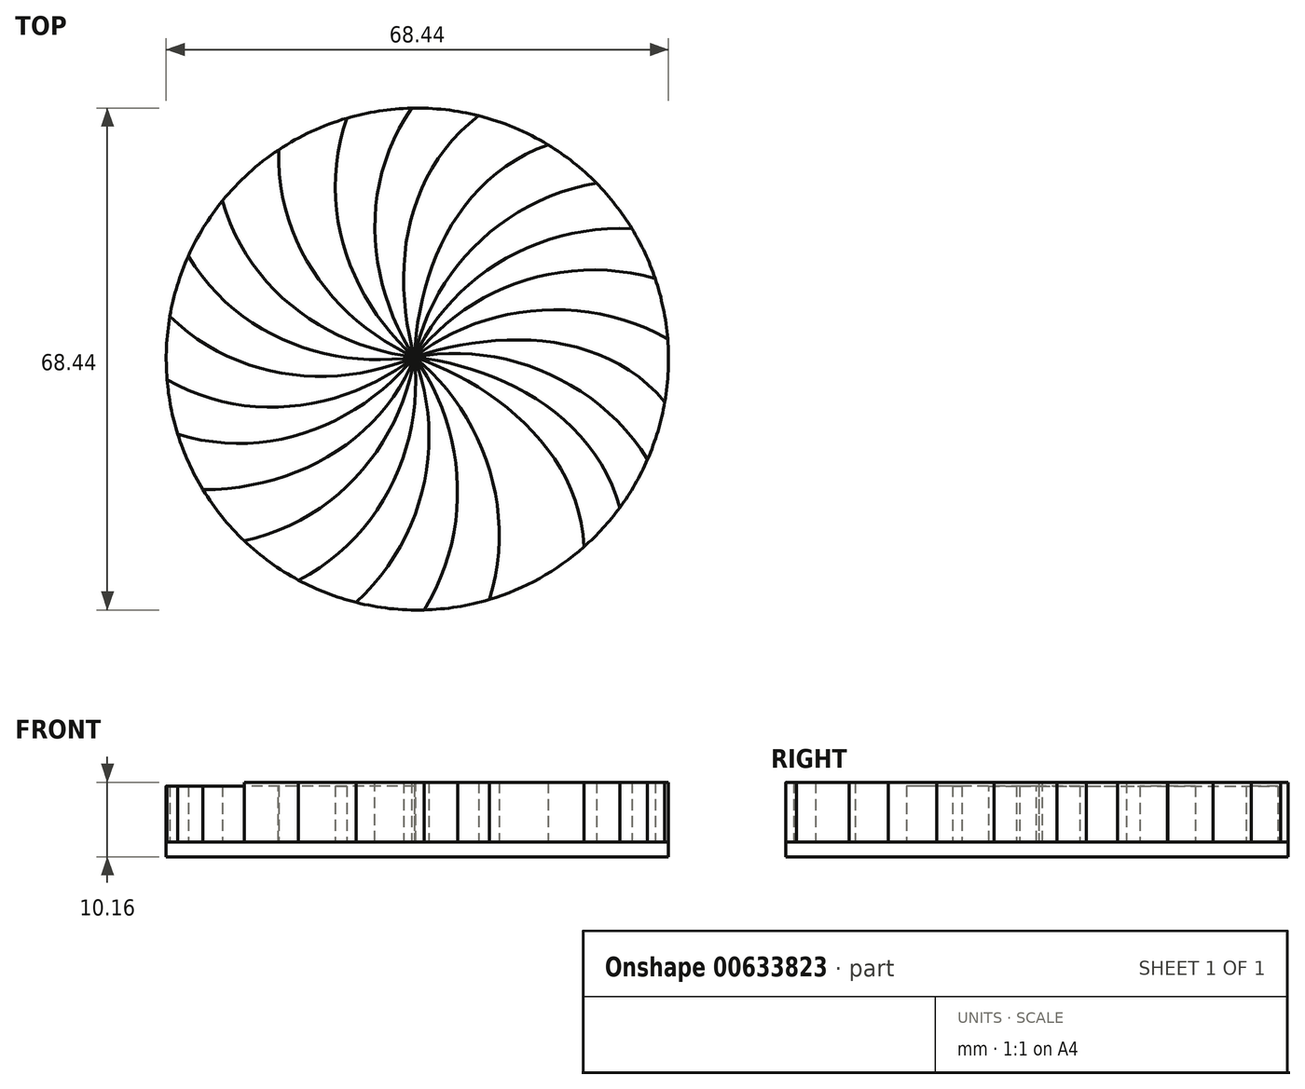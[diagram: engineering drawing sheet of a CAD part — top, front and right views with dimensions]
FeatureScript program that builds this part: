
annotation { "Feature Type Name" : "Feature", "Feature Type Description" : "" }
export const myFeature = defineFeature(function(context is Context, id is Id, definition is map)
    precondition{}
    {
        {
            var Q0;
            Q0=qCreatedBy(makeId("Top.planeOp"),FACE);
            var sketch = newSketch(context, id + "F0", { "sketchPlane" : qUnion([Q0])});
            skCircle(sketch, "E0", {"center": v(0, 0) * mm, "radius": 34.22 * mm});
            skSolve(sketch);
        }
        {
            var Q0;
            Q0=makeQuery(id+"F0.imprint","IMPRINT",FACE,{"disambiguationData":[TD([[makeQuery(id+"F0.imprint","IMPRINT",EDGE,{"derivedFrom":sQuery(id+"F0.wireOp",EDGE,"E0")}),1.0]])]});
            extrude(context, id + "F1", {"entities" : qUnion([Q0]), "depth" : 2.03 * mm, "offsetDistance" : 25.4 * mm});
        }
        {
            var Q0;
            Q0=makeQuery(id+"F1.opExtrude","CAP_FACE",FACE,{"disambiguationData":[OSD([sQuery(id+"F0.wireOp",EDGE,"E0")])],"isStart":false});
            var sketch = newSketch(context, id + "F2", { "sketchPlane" : qUnion([Q0])});
            skFitSpline(sketch, "E1", {"points": [v(-0.38, 0.28) * mm, v(-18.88, 29) * mm], "startDerivative": vector(-32.94, 14.89) * mm, "endDerivative": vector(1.8, 38.8) * mm});
            skFitSpline(sketch, "E2", {"points": [v(-0.38, 0.28) * mm, v(-9.47, 33.21) * mm], "startDerivative": vector(-27, 24.04) * mm, "endDerivative": vector(13.3, 36.5) * mm});
            skFitSpline(sketch, "E3", {"points": [v(-0.38, 0.28) * mm, v(8.37, 33.18) * mm], "startDerivative": vector(-9.77, 34.8) * mm, "endDerivative": vector(30.88, 23.56) * mm});
            skFitSpline(sketch, "E4", {"points": [v(-0.38, 0.28) * mm, v(-26.71, 22.05) * mm], "startDerivative": vector(-35.9, 4.21) * mm, "endDerivative": vector(-10.04, 37.53) * mm});
            skFitSpline(sketch, "E5", {"points": [v(-0.38, 0.28) * mm, v(17.81, 29.22) * mm], "startDerivative": vector(1.4, 36.12) * mm, "endDerivative": vector(36.63, 12.94) * mm});
            skFitSpline(sketch, "E6", {"points": [v(-0.38, 0.28) * mm, v(-31.46, 14.47) * mm], "startDerivative": vector(-35.76, -5.25) * mm, "endDerivative": vector(-19.43, 33.63) * mm});
            skFitSpline(sketch, "E7", {"points": [v(-0.38, 0.28) * mm, v(-34.04, 6.17) * mm], "startDerivative": vector(-33.28, -14.1) * mm, "endDerivative": vector(-27.29, 27.65) * mm});
            skFitSpline(sketch, "E8", {"points": [v(-0.38, 0.28) * mm, v(9.78, -32.94) * mm], "startDerivative": vector(27.96, -22.9) * mm, "endDerivative": vector(-11.79, -37.01) * mm});
            skFitSpline(sketch, "E9", {"points": [v(-0.38, 0.28) * mm, v(0.75, -34.44) * mm], "startDerivative": vector(21.08, -29.36) * mm, "endDerivative": vector(-20.96, -32.7) * mm});
            skFitSpline(sketch, "E10", {"points": [v(-0.38, 0.28) * mm, v(-8.37, -33.18) * mm], "startDerivative": vector(12.76, -33.82) * mm, "endDerivative": vector(-28.71, -26.16) * mm});
            skFitSpline(sketch, "E11", {"points": [v(-0.38, 0.28) * mm, v(-16.18, -30.15) * mm], "startDerivative": vector(3.57, -35.97) * mm, "endDerivative": vector(-34.5, -17.84) * mm});
            skFitSpline(sketch, "E12", {"points": [v(-0.38, 0.28) * mm, v(-23.6, -24.78) * mm], "startDerivative": vector(-5.86, -35.67) * mm, "endDerivative": vector(-37.95, -8.3) * mm});
            skFitSpline(sketch, "E13", {"points": [v(-0.38, 0.28) * mm, v(-29.22, -17.81) * mm], "startDerivative": vector(-13.16, -33.66) * mm, "endDerivative": vector(-38.84, -0.2) * mm});
            skFitSpline(sketch, "E14", {"points": [v(-0.38, 0.28) * mm, v(-34.43, -2.6) * mm], "startDerivative": vector(-28.6, -22.1) * mm, "endDerivative": vector(-33.42, 19.79) * mm});
            skFitSpline(sketch, "E15", {"points": [v(-0.38, 0.28) * mm, v(-32.92, -10.16) * mm], "startDerivative": vector(-22.9, -27.96) * mm, "endDerivative": vector(-37.01, 11.79) * mm});
            skFitSpline(sketch, "E16", {"points": [v(-0.38, 0.28) * mm, v(24.4, 24) * mm], "startDerivative": vector(7.38, 35.38) * mm, "endDerivative": vector(38.27, 6.66) * mm});
            skFitSpline(sketch, "E17", {"points": [v(-0.38, 0.28) * mm, v(29.24, 17.78) * mm], "startDerivative": vector(14.89, 32.94) * mm, "endDerivative": vector(38.8, -1.8) * mm});
            skFitSpline(sketch, "E18", {"points": [v(-0.38, 0.28) * mm, v(32.4, 11) * mm], "startDerivative": vector(21.88, 28.77) * mm, "endDerivative": vector(37.42, -10.44) * mm});
            skFitSpline(sketch, "E19", {"points": [v(-0.38, 0.28) * mm, v(33.72, -5.84) * mm], "startDerivative": vector(34.32, 11.35) * mm, "endDerivative": vector(24.95, -29.77) * mm});
            skFitSpline(sketch, "E20", {"points": [v(-0.38, 0.28) * mm, v(34.44, 2.56) * mm], "startDerivative": vector(28.46, 22.29) * mm, "endDerivative": vector(33.55, -19.58) * mm});
            skFitSpline(sketch, "E21", {"points": [v(-0.38, 0.28) * mm, v(31.38, -13.66) * mm], "startDerivative": vector(35.52, 6.7) * mm, "endDerivative": vector(20.78, -32.82) * mm});
            skFitSpline(sketch, "E22", {"points": [v(-0.38, 0.28) * mm, v(27.57, -20.27) * mm], "startDerivative": vector(35.9, -4.22) * mm, "endDerivative": vector(10.02, -37.53) * mm});
            skFitSpline(sketch, "E23", {"points": [v(-0.38, 0.28) * mm, v(22.7, -25.72) * mm], "startDerivative": vector(34.1, -11.96) * mm, "endDerivative": vector(1.58, -38.81) * mm});
            skFitSpline(sketch, "E24", {"points": [v(-0.38, 0.28) * mm, v(17, -29.33) * mm], "startDerivative": vector(31.51, -17.7) * mm, "endDerivative": vector(-5.18, -38.5) * mm});
            skFitSpline(sketch, "E25", {"points": [v(-0.38, 0.28) * mm, v(-0.63, 34.44) * mm], "startDerivative": vector(-19.85, 30.2) * mm, "endDerivative": vector(22.3, 31.81) * mm});
            skSolve(sketch);
        }
        {
            var Q0;
            {var subQ1=sQuery(id+"F2.wireOp",EDGE,"E7");var subQ3=makeQuery(id+"F1.opExtrude","CAP_EDGE",EDGE,{"disambiguationData":[OSD([sQuery(id+"F0.wireOp",EDGE,"E0")])],"isStart":false});var subQ4=makeQuery(id+"F2.imprint","INTERSECT",VERTEX,{"derivedFrom":[subQ3,subQ1]});Q0=makeQuery(id+"F2.imprint","IMPRINT",FACE,{"disambiguationData":[TD([[makeQuery(id+"F2.imprint","IMPRINT",EDGE,{"disambiguationData":[TD([[subQ4,-1.0]])],"derivedFrom":subQ3}),1.0]])]});}
            var Q1;
            {var subQ1=sQuery(id+"F2.wireOp",EDGE,"E4");var subQ3=makeQuery(id+"F1.opExtrude","CAP_EDGE",EDGE,{"disambiguationData":[OSD([sQuery(id+"F0.wireOp",EDGE,"E0")])],"isStart":false});var subQ4=makeQuery(id+"F2.imprint","INTERSECT",VERTEX,{"derivedFrom":[subQ3,subQ1]});Q1=makeQuery(id+"F2.imprint","IMPRINT",FACE,{"disambiguationData":[TD([[makeQuery(id+"F2.imprint","IMPRINT",EDGE,{"disambiguationData":[TD([[subQ4,-1.0]])],"derivedFrom":subQ3}),1.0]])]});}
            var Q2;
            {var subQ1=sQuery(id+"F2.wireOp",EDGE,"E1");var subQ3=makeQuery(id+"F1.opExtrude","CAP_EDGE",EDGE,{"disambiguationData":[OSD([sQuery(id+"F0.wireOp",EDGE,"E0")])],"isStart":false});var subQ4=makeQuery(id+"F2.imprint","INTERSECT",VERTEX,{"derivedFrom":[subQ3,subQ1]});Q2=makeQuery(id+"F2.imprint","IMPRINT",FACE,{"disambiguationData":[TD([[makeQuery(id+"F2.imprint","IMPRINT",EDGE,{"disambiguationData":[TD([[subQ4,1.0]])],"derivedFrom":subQ3}),1.0]])]});}
            var Q3;
            {var subQ1=sQuery(id+"F2.wireOp",EDGE,"E13");var subQ3=makeQuery(id+"F1.opExtrude","CAP_EDGE",EDGE,{"disambiguationData":[OSD([sQuery(id+"F0.wireOp",EDGE,"E0")])],"isStart":false});var subQ4=makeQuery(id+"F2.imprint","INTERSECT",VERTEX,{"derivedFrom":[subQ3,subQ1]});Q3=makeQuery(id+"F2.imprint","IMPRINT",FACE,{"disambiguationData":[TD([[makeQuery(id+"F2.imprint","IMPRINT",EDGE,{"disambiguationData":[TD([[subQ4,1.0]])],"derivedFrom":subQ3}),1.0]])]});}
            var Q4;
            Q4=sQuery(id+"F2.wireOp",EDGE,"E16");
            var Q5;
            Q5=sQuery(id+"F2.wireOp",EDGE,"E5");
            var Q6;
            Q6=sQuery(id+"F2.wireOp",EDGE,"E3");
            var Q7;
            Q7=sQuery(id+"F2.wireOp",EDGE,"E25");
            var Q8;
            Q8=sQuery(id+"F2.wireOp",EDGE,"E2");
            var Q9;
            Q9=sQuery(id+"F2.wireOp",EDGE,"E1");
            var Q10;
            Q10=sQuery(id+"F2.wireOp",EDGE,"E4");
            var Q11;
            Q11=sQuery(id+"F2.wireOp",EDGE,"E6");
            var Q12;
            Q12=sQuery(id+"F2.wireOp",EDGE,"E7");
            var Q13;
            Q13=sQuery(id+"F2.wireOp",EDGE,"E14");
            var Q14;
            Q14=sQuery(id+"F2.wireOp",EDGE,"E15");
            var Q15;
            Q15=sQuery(id+"F2.wireOp",EDGE,"E13");
            var Q16;
            Q16=sQuery(id+"F2.wireOp",EDGE,"E12");
            var Q17;
            Q17=sQuery(id+"F2.wireOp",EDGE,"E11");
            var Q18;
            Q18=sQuery(id+"F2.wireOp",EDGE,"E10");
            var Q19;
            Q19=sQuery(id+"F2.wireOp",EDGE,"E9");
            var Q20;
            Q20=sQuery(id+"F2.wireOp",EDGE,"E8");
            var Q21;
            Q21=sQuery(id+"F2.wireOp",EDGE,"E24");
            var Q22;
            Q22=sQuery(id+"F2.wireOp",EDGE,"E23");
            var Q23;
            Q23=sQuery(id+"F2.wireOp",EDGE,"E22");
            var Q24;
            Q24=sQuery(id+"F2.wireOp",EDGE,"E21");
            var Q25;
            Q25=sQuery(id+"F2.wireOp",EDGE,"E19");
            var Q26;
            Q26=sQuery(id+"F2.wireOp",EDGE,"E20");
            var Q27;
            Q27=sQuery(id+"F2.wireOp",EDGE,"E18");
            var Q28;
            Q28=sQuery(id+"F2.wireOp",EDGE,"E17");
            extrude(context, id + "F3", {"entities" : qUnion([Q0, Q1, Q2, Q3]), "surfaceEntities" : qUnion([Q4, Q5, Q6, Q7, Q8, Q9, Q10, Q11, Q12, Q13, Q14, Q15, Q16, Q17, Q18, Q19, Q20, Q21, Q22, Q23, Q24, Q25, Q26, Q27, Q28]), "depth" : 7.62 * mm, "offsetDistance" : 25.4 * mm});
        }
        {
            var Q0;
            {var subQ0=sQuery(id+"F2.wireOp",EDGE,"E5");Q0=makeQuery(id+"F2.imprint","IMPRINT",FACE,{"disambiguationData":[TD([[makeQuery(id+"F2.imprint","IMPRINT",EDGE,{"derivedFrom":subQ0}),-1.0]])]});}
            var Q1;
            {var subQ0=sQuery(id+"F2.wireOp",EDGE,"E3");Q1=makeQuery(id+"F2.imprint","IMPRINT",FACE,{"disambiguationData":[TD([[makeQuery(id+"F2.imprint","IMPRINT",EDGE,{"derivedFrom":subQ0}),1.0]])]});}
            var Q2;
            {var subQ0=sQuery(id+"F2.wireOp",EDGE,"E17");Q2=makeQuery(id+"F2.imprint","IMPRINT",FACE,{"disambiguationData":[TD([[makeQuery(id+"F2.imprint","IMPRINT",EDGE,{"derivedFrom":subQ0}),-1.0]])]});}
            var Q3;
            {var subQ0=sQuery(id+"F2.wireOp",EDGE,"E19");Q3=makeQuery(id+"F2.imprint","IMPRINT",FACE,{"disambiguationData":[TD([[makeQuery(id+"F2.imprint","IMPRINT",EDGE,{"derivedFrom":subQ0}),1.0]])]});}
            var Q4;
            {var subQ0=sQuery(id+"F2.wireOp",EDGE,"E21");Q4=makeQuery(id+"F2.imprint","IMPRINT",FACE,{"disambiguationData":[TD([[makeQuery(id+"F2.imprint","IMPRINT",EDGE,{"derivedFrom":subQ0}),-1.0]])]});}
            var Q5;
            {var subQ1=sQuery(id+"F2.wireOp",EDGE,"E8");var subQ3=makeQuery(id+"F1.opExtrude","CAP_EDGE",EDGE,{"disambiguationData":[OSD([sQuery(id+"F0.wireOp",EDGE,"E0")])],"isStart":false});var subQ4=makeQuery(id+"F2.imprint","INTERSECT",VERTEX,{"derivedFrom":[subQ3,subQ1]});Q5=makeQuery(id+"F2.imprint","IMPRINT",FACE,{"disambiguationData":[TD([[makeQuery(id+"F2.imprint","IMPRINT",EDGE,{"disambiguationData":[TD([[subQ4,-1.0]])],"derivedFrom":subQ3}),1.0]])]});}
            var Q6;
            {var subQ0=sQuery(id+"F2.wireOp",EDGE,"E10");Q6=makeQuery(id+"F2.imprint","IMPRINT",FACE,{"disambiguationData":[TD([[makeQuery(id+"F2.imprint","IMPRINT",EDGE,{"derivedFrom":subQ0}),1.0]])]});}
            var Q7;
            {var subQ0=sQuery(id+"F2.wireOp",EDGE,"E11");Q7=makeQuery(id+"F2.imprint","IMPRINT",FACE,{"disambiguationData":[TD([[makeQuery(id+"F2.imprint","IMPRINT",EDGE,{"derivedFrom":subQ0}),-1.0]])]});}
            extrude(context, id + "F4", {"entities" : qUnion([Q0, Q1, Q2, Q3, Q4, Q5, Q6, Q7]), "depth" : 8.13 * mm, "offsetDistance" : 25.4 * mm});
        }
    });
